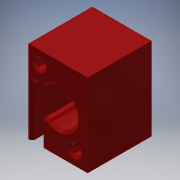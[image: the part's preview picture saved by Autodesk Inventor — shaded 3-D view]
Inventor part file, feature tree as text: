
AUTODESK INVENTOR PART (.ipt)
format: ipt  version: 2019 (Build 230136000, 136)  size: 182,784 bytes
history: native  units: mm
features: sketch x4, extrude x3, fillet x1, hole x1, chamfer x1, projected_geometry x1
ambient origin geometry x8: Origin, YZ Plane, XZ Plane, XY Plane, X Axis, Y Axis, Z Axis, Center Point
bodies: Solid1 (feature_tree)
feature tree (11):
  extrude  "Extrusion1"  Depth=35.0mm
  extrude  "Extrusion2"  Depth=12.0mm
  extrude  "Extrusion3"  Depth=10.0mm
  fillet  "Fillet1"  Radius=11.0mm
  hole  "Hole1"  [1 undecoded]
  chamfer  "Chamfer1"  Distance=15.0mm
  sketch  "Sketch1"  dims[d0=25.0mm d1=35.0mm]
  sketch  "Sketch2"  dims[d2=12.0mm d3=0.0mm d4=6.1mm]
  sketch  "Sketch4"  dims[d5=10.0mm d6=0.0mm d9=15.3mm d10=11.0mm]
  projected_geometry  "Projected Loop2"
  sketch  "Sketch5"  dims[d11=7.0mm d12=5.0mm d13=15.0mm d14=0.0mm d15=2.0mm d16=12.5mm d17=7.0mm d18=12.0mm d19=12.0mm d20=8.0mm d21=4.2mm d22=3.2mm d23=6.0mm d24=2.0mm d25=90.0deg d26=8.0mm d27=20.594885mm d28=1.0mm d29=2.0mm d30=45.0deg]
note: 1 required parameter value undecoded (feature->parameter linkage not recoverable at this tier; creation-order binding heuristic only, values carry confidence <= 0.55)
